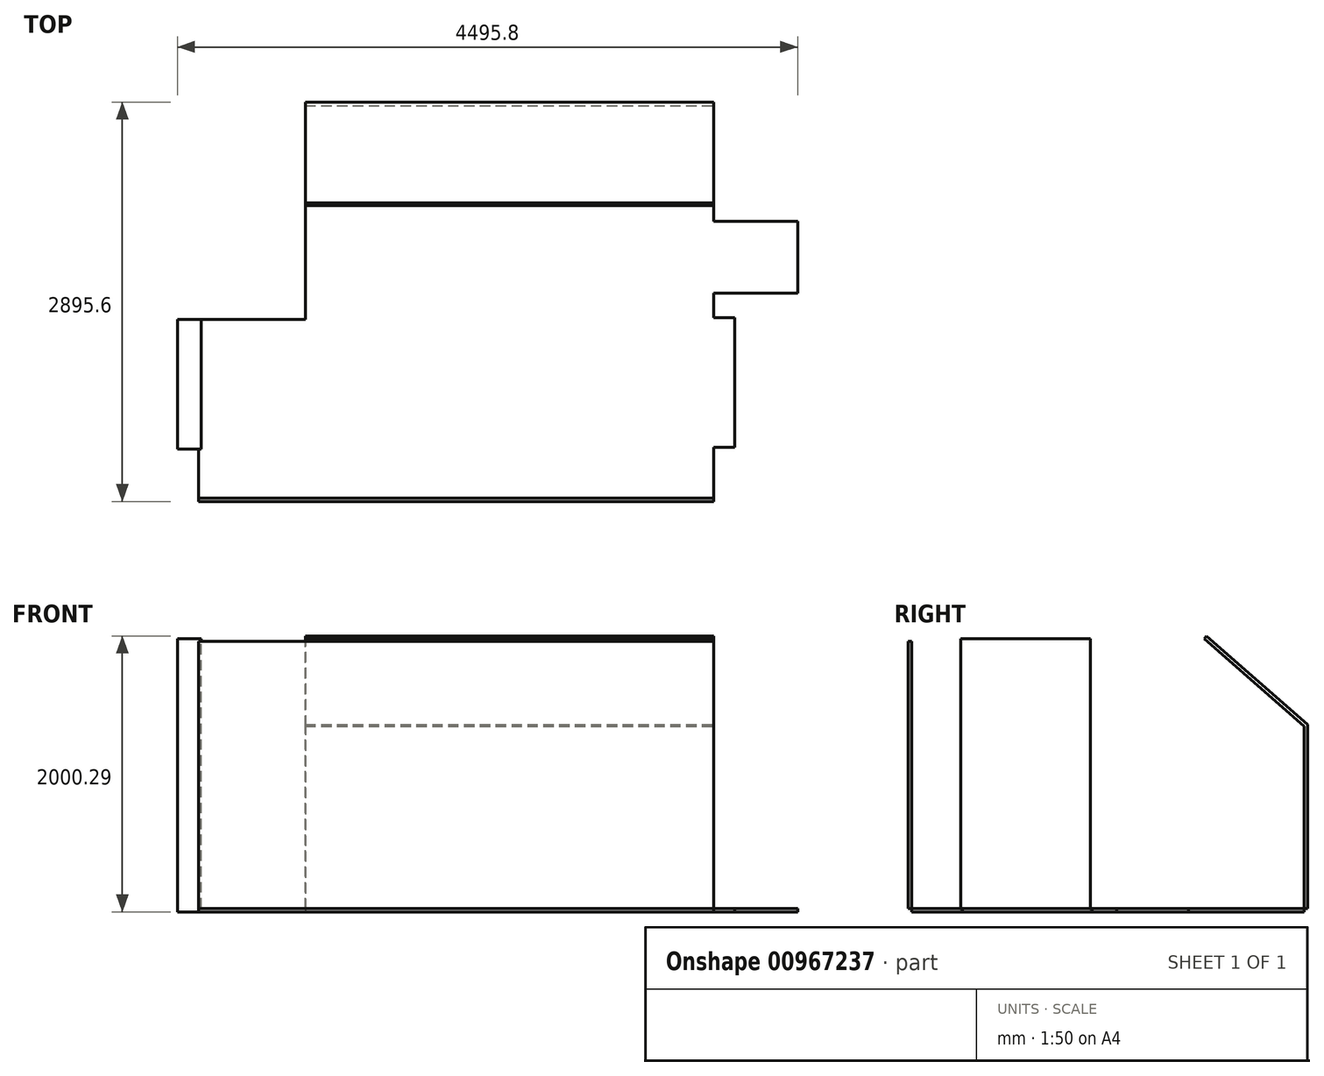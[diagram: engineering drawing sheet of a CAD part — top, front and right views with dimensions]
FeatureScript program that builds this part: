
annotation { "Feature Type Name" : "Feature", "Feature Type Description" : "" }
export const myFeature = defineFeature(function(context is Context, id is Id, definition is map)
    precondition{}
    {
        {
            var Q0;
            Q0=qCreatedBy(makeId("Top.planeOp"),FACE);
            var sketch = newSketch(context, id + "F0", { "sketchPlane" : qUnion([Q0])});
            skLineSegment(sketch, "E0.top", {"start": v(0, 2844.8) * mm, "end": v(2959.1, 2844.8) * mm});
            skLineSegment(sketch, "E0.left", {"start": v(0, 1295.4) * mm, "end": v(0, 2844.8) * mm});
            skLineSegment(sketch, "E0.right", {"start": v(2959.1, 0) * mm, "end": v(2959.1, 368.3) * mm});
            skLineSegment(sketch, "E1.right", {"start": v(-774.7, 355.6) * mm, "end": v(-774.7, 0) * mm});
            skLineSegment(sketch, "E2", {"start": v(-774.7, 0) * mm, "end": v(2959.1, 0) * mm});
            skLineSegment(sketch, "E3", {"start": v(2959.1, 1308.1) * mm, "end": v(3111.5, 1308.1) * mm});
            skLineSegment(sketch, "E4", {"start": v(3111.5, 1308.1) * mm, "end": v(3111.5, 368.3) * mm});
            skLineSegment(sketch, "E5", {"start": v(3111.5, 368.3) * mm, "end": v(2959.1, 368.3) * mm});
            skLineSegment(sketch, "E6.trimOffspring", {"start": v(2959.1, 1308.1) * mm, "end": v(2959.1, 1485.9) * mm});
            skLineSegment(sketch, "E7.top", {"start": v(-774.7, 355.6) * mm, "end": v(-927.1, 355.6) * mm});
            skLineSegment(sketch, "E7.right", {"start": v(-927.1, 1295.4) * mm, "end": v(-927.1, 355.6) * mm});
            skLineSegment(sketch, "E8", {"start": v(-927.1, 1295.4) * mm, "end": v(0, 1295.4) * mm});
            skLineSegment(sketch, "E9.bottom", {"start": v(2959.1, 2006.6) * mm, "end": v(3568.7, 2006.6) * mm});
            skLineSegment(sketch, "E9.top", {"start": v(2959.1, 1485.9) * mm, "end": v(3568.7, 1485.9) * mm});
            skLineSegment(sketch, "E9.right", {"start": v(3568.7, 2006.6) * mm, "end": v(3568.7, 1485.9) * mm});
            skLineSegment(sketch, "E10.trimOffspring", {"start": v(2959.1, 2006.6) * mm, "end": v(2959.1, 2844.8) * mm});
            skSolve(sketch);
        }
        {
            var Q0;
            Q0=makeQuery(id+"F0.imprint","IMPRINT",FACE,{"disambiguationData":[TD([[makeQuery(id+"F0.imprint","IMPRINT",EDGE,{"derivedFrom":sQuery(id+"F0.wireOp",EDGE,"E0.top")}),-1.0]])]});
            extrude(context, id + "F1", {"entities" : qUnion([Q0]), "depth" : 25.4 * mm, "offsetDistance" : 25.4 * mm});
        }
        {
            var Q0;
            Q0=makeQuery(id+"F1.opExtrude","SWEPT_FACE",FACE,{"disambiguationData":[OSD([sQuery(id+"F0.wireOp",EDGE,"E2")])]});
            var sketch = newSketch(context, id + "F2", { "sketchPlane" : qUnion([Q0])});
            skLineSegment(sketch, "E11.bottom", {"start": v(2959.1, 25.4) * mm, "end": v(-774.7, 25.4) * mm});
            skLineSegment(sketch, "E11.top", {"start": v(2959.1, 1962.15) * mm, "end": v(-774.7, 1962.15) * mm});
            skLineSegment(sketch, "E11.left", {"start": v(2959.1, 25.4) * mm, "end": v(2959.1, 1962.15) * mm});
            skLineSegment(sketch, "E11.right", {"start": v(-774.7, 25.4) * mm, "end": v(-774.7, 1962.15) * mm});
            skSolve(sketch);
        }
        {
            var Q0;
            Q0=makeQuery(id+"F2.imprint","IMPRINT",FACE,{"disambiguationData":[TD([[makeQuery(id+"F2.imprint","IMPRINT",EDGE,{"derivedFrom":sQuery(id+"F2.wireOp",EDGE,"E11.bottom")}),1.0]])]});
            extrude(context, id + "F3", {"entities" : qUnion([Q0]), "depth" : 25.4 * mm, "offsetDistance" : 25.4 * mm});
        }
        {
            var Q0;
            Q0=makeQuery(id+"F1.opExtrude","SWEPT_FACE",FACE,{"disambiguationData":[OSD([sQuery(id+"F0.wireOp",EDGE,"E7.right")])]});
            var sketch = newSketch(context, id + "F4", { "sketchPlane" : qUnion([Q0])});
            skLineSegment(sketch, "E12.bottom", {"start": v(-355.6, 25.4) * mm, "end": v(-1295.4, 25.4) * mm});
            skLineSegment(sketch, "E12.top", {"start": v(-355.6, 1981.2) * mm, "end": v(-1295.4, 1981.2) * mm});
            skLineSegment(sketch, "E12.left", {"start": v(-355.6, 25.4) * mm, "end": v(-355.6, 1981.2) * mm});
            skLineSegment(sketch, "E12.right", {"start": v(-1295.4, 25.4) * mm, "end": v(-1295.4, 1981.2) * mm});
            skSolve(sketch);
        }
        {
            var Q0;
            Q0=makeQuery(id+"F4.imprint","IMPRINT",FACE,{"disambiguationData":[TD([[makeQuery(id+"F4.imprint","IMPRINT",EDGE,{"derivedFrom":sQuery(id+"F4.wireOp",EDGE,"E12.bottom")}),1.0]])]});
            extrude(context, id + "F5", {"entities" : qUnion([Q0]), "operationType" : NewBodyOperationType.ADD, "oppositeDirection" : true, "depth" : 171.45 * mm, "offsetDistance" : 25.4 * mm});
        }
        {
            var Q0;
            Q0=makeQuery(id+"F1.opExtrude","SWEPT_FACE",FACE,{"disambiguationData":[OSD([sQuery(id+"F0.wireOp",EDGE,"E6.trimOffspring")])]});
            var sketch = newSketch(context, id + "F6", { "sketchPlane" : qUnion([Q0])});
            skLineSegment(sketch, "E13", {"start": v(2844.8, 25.4) * mm, "end": v(2844.8, 1346.2) * mm});
            skLineSegment(sketch, "E14", {"start": v(2844.8, 1346.2) * mm, "end": v(2120.9, 1981.2) * mm});
            skLineSegment(sketch, "E15", {"start": v(2120.9, 1981.2) * mm, "end": v(2137.65, 2000.3) * mm});
            skLineSegment(sketch, "E16", {"start": v(2137.65, 2000.3) * mm, "end": v(2870.2, 1357.7) * mm});
            skLineSegment(sketch, "E17", {"start": v(2870.2, 1357.7) * mm, "end": v(2870.2, 25.4) * mm});
            skLineSegment(sketch, "E18", {"start": v(2870.2, 25.4) * mm, "end": v(2844.8, 25.4) * mm});
            skSolve(sketch);
        }
        {
            var Q0;
            Q0 = qSketchRegion(id + "F6", true);
            var Q1;
            Q1=makeQuery(id+"F1.opExtrude","SWEPT_FACE",FACE,{"disambiguationData":[OSD([sQuery(id+"F0.wireOp",EDGE,"E0.left")])]});
            extrude(context, id + "F7", {"entities" : qUnion([Q0]), "oppositeDirection" : true, "depth" : 2959.1 * mm, "endBoundEntityFace" : qUnion([Q1]), "offsetDistance" : 25.4 * mm});
        }
    });
